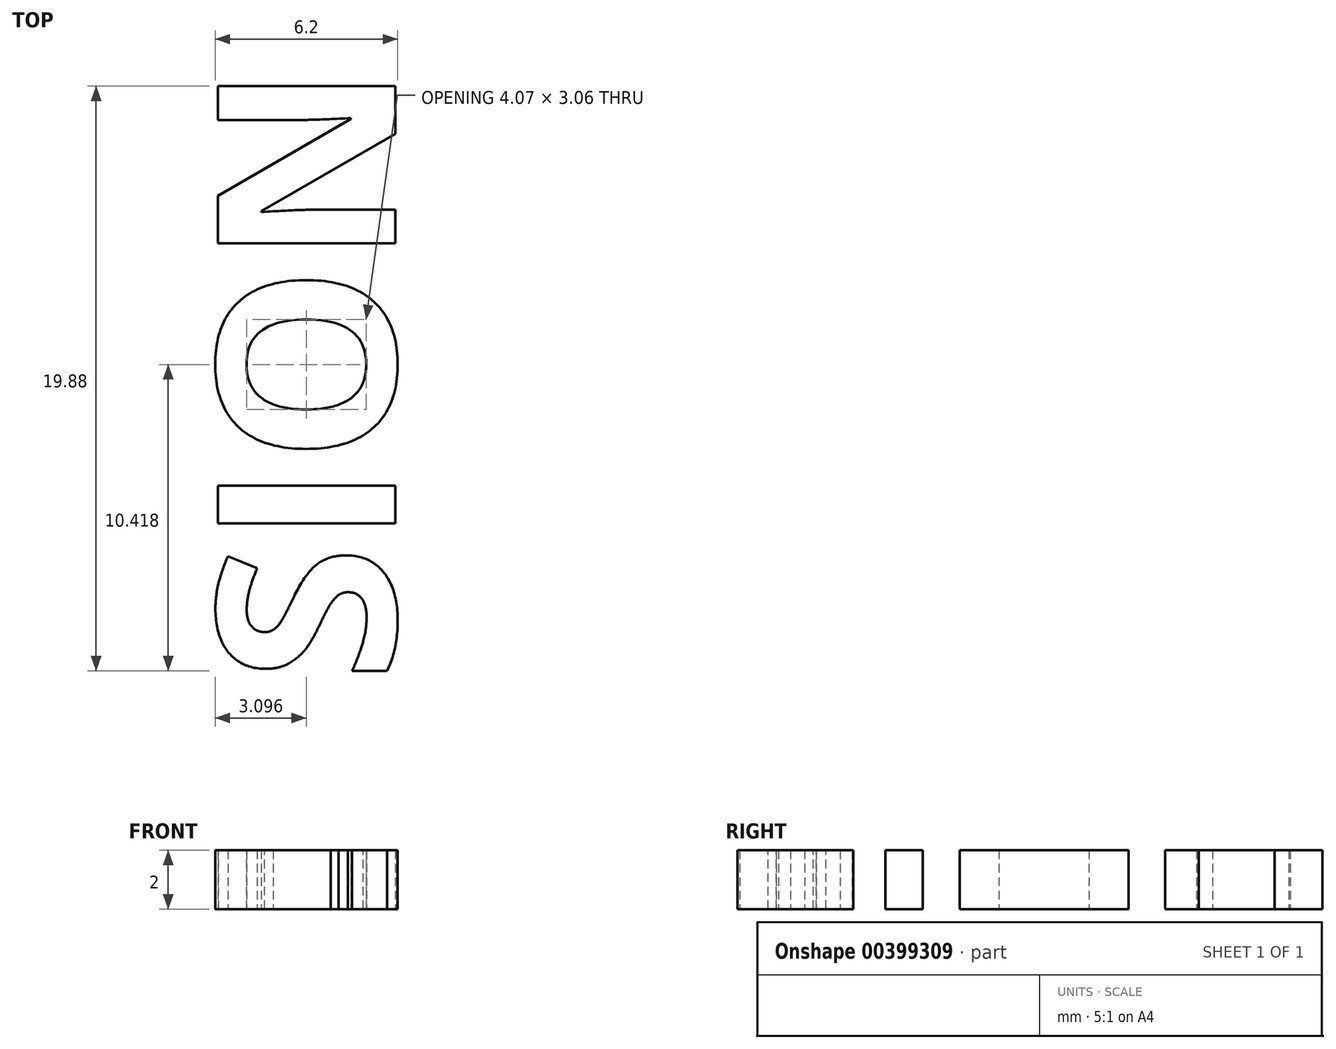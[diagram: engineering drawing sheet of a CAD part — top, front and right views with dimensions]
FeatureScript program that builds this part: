
annotation { "Feature Type Name" : "Feature", "Feature Type Description" : "" }
export const myFeature = defineFeature(function(context is Context, id is Id, definition is map)
    precondition{}
    {
        {
            var Q0;
            Q0=qCreatedBy(makeId("Top.planeOp"),FACE);
            var sketch = newSketch(context, id + "F0", { "sketchPlane" : qUnion([Q0])});
            skText(sketch, "E0", { "text": "SION", "fontName": "OpenSans-Bold.ttf"});
            const initialGuessF0  = {"E0": [-0.02273, -0.06928, 0, 1, 0.00608]};
            skSetInitialGuess(sketch, initialGuessF0);
            skSolve(sketch);
        }
        {
            var Q0;
            Q0 = qSketchRegion(id + "F0", true);
            extrude(context, id + "F1", {"entities" : qUnion([Q0]), "depth" : 2 * mm, "offsetDistance" : 25 * mm});
        }
    });
